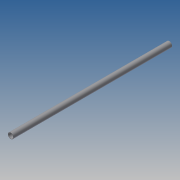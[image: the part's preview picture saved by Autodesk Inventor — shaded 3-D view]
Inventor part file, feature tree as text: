
AUTODESK INVENTOR PART (.ipt)
format: ipt  version: 2014 SP1 (Build 180222100, 222)  size: 71,680 bytes
history: native  units: in
note: dims shown in document units (in); Inventor stores cm internally (conversion verified against a paired STEP export)
features: extrude x1, sketch x1
ambient origin geometry x8: Origin, YZ Plane, XZ Plane, XY Plane, X Axis, Y Axis, Z Axis, Center Point
bodies: Solid1 (feature_tree)
feature tree (2):
  extrude  "Extrusion1"  Depth=59.0551in
  sketch  "Sketch1"  dims[d0=1.8504in d1=0.1181in d2=59.0551in d3=0.0in]
